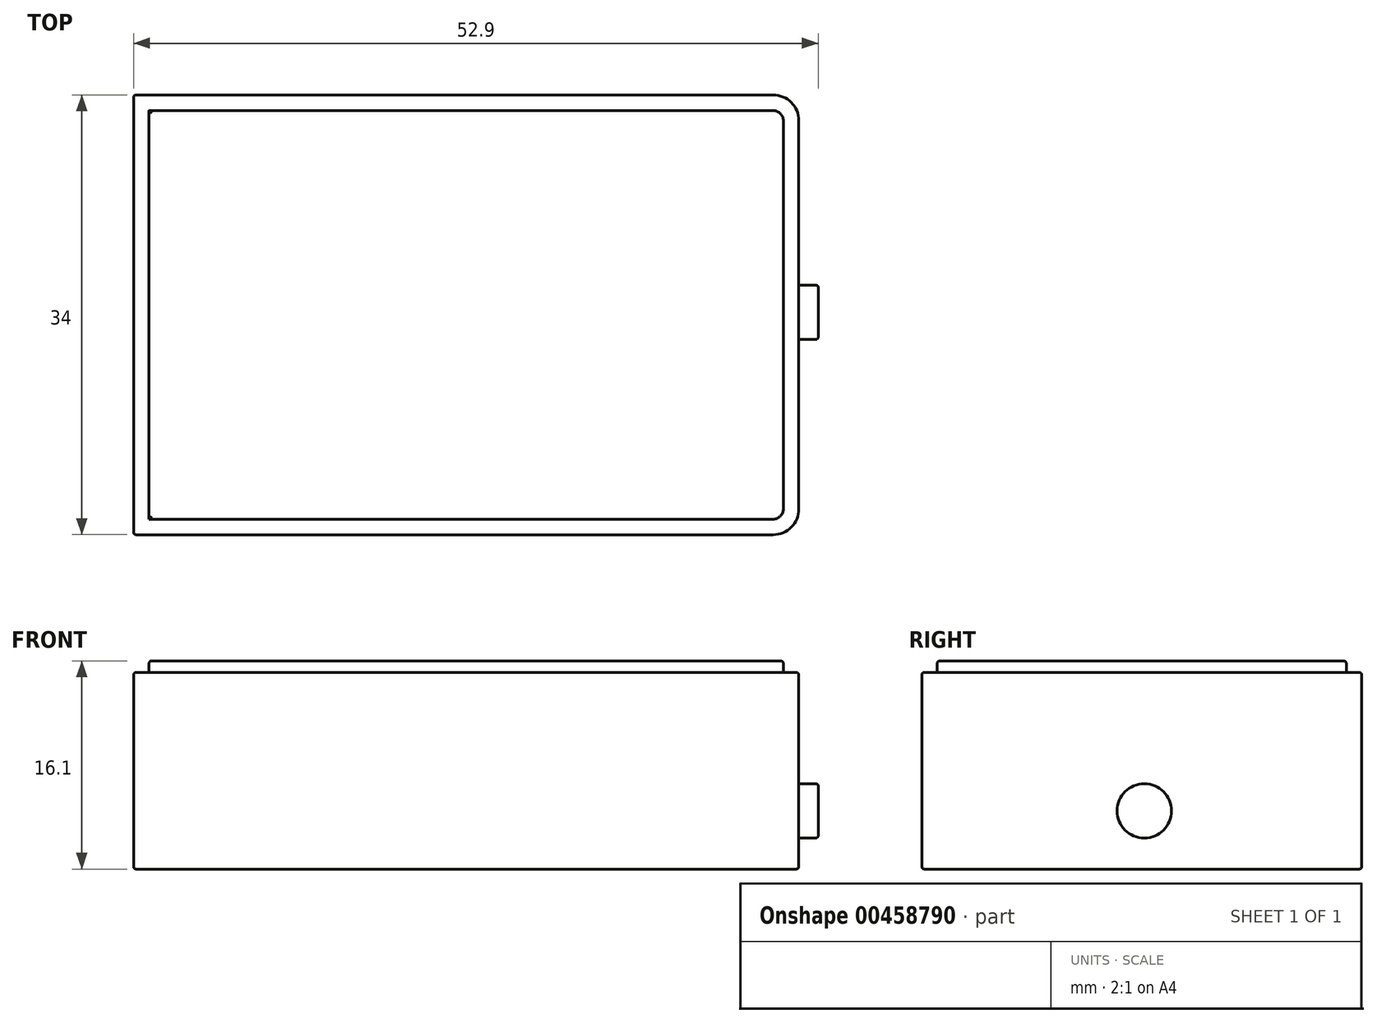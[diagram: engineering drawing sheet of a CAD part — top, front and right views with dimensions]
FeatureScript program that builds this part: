
annotation { "Feature Type Name" : "Feature", "Feature Type Description" : "" }
export const myFeature = defineFeature(function(context is Context, id is Id, definition is map)
    precondition{}
    {
        {
            var Q0;
            Q0=qCreatedBy(makeId("Top.planeOp"),FACE);
            var sketch = newSketch(context, id + "F0", { "sketchPlane" : qUnion([Q0])});
            skLineSegment(sketch, "E0.bottom", {"start": v(-30.33, 20.45) * mm, "end": v(19.07, 20.45) * mm});
            skLineSegment(sketch, "E0.top", {"start": v(-30.33, -13.55) * mm, "end": v(19.07, -13.55) * mm});
            skLineSegment(sketch, "E0.left", {"start": v(-30.33, 20.45) * mm, "end": v(-30.33, -13.55) * mm});
            skLineSegment(sketch, "E0.right", {"start": v(21.07, 18.45) * mm, "end": v(21.07, -11.55) * mm});
            skPoint(sketch, "E1.visualSharp", {"position": v(21.07, 20.45) * mm});
            skArc(sketch, "E1.filletArc", {"start": v(21.07, 18.45) * mm, "mid": v(20.49, 19.86) * mm, "end": v(19.07, 20.45) * mm});
            skPoint(sketch, "E2.visualSharp", {"position": v(21.07, -13.55) * mm});
            skArc(sketch, "E2.filletArc", {"start": v(19.07, -13.55) * mm, "mid": v(20.49, -12.97) * mm, "end": v(21.07, -11.55) * mm});
            skSolve(sketch);
        }
        {
            var Q0;
            Q0=makeQuery(id+"F0.imprint","IMPRINT",FACE,{"disambiguationData":[TD([[makeQuery(id+"F0.imprint","IMPRINT",EDGE,{"derivedFrom":sQuery(id+"F0.wireOp",EDGE,"E0.bottom")}),-1.0]])]});
            extrude(context, id + "F1", {"entities" : qUnion([Q0]), "depth" : 15.2 * mm, "offsetDistance" : 25 * mm});
        }
        {
            var Q0;
            Q0=makeQuery(id+"F1.opExtrude","SWEPT_FACE",FACE,{"disambiguationData":[OSD([sQuery(id+"F0.wireOp",EDGE,"E0.right")])]});
            var sketch = newSketch(context, id + "F2", { "sketchPlane" : qUnion([Q0])});
            skCircle(sketch, "E3", {"center": v(3.65, 4.5) * mm, "radius": 2.1 * mm});
            skSolve(sketch);
        }
        {
            var Q0;
            Q0=makeQuery(id+"F2.imprint","IMPRINT",FACE,{"disambiguationData":[TD([[makeQuery(id+"F2.imprint","IMPRINT",EDGE,{"derivedFrom":sQuery(id+"F2.wireOp",EDGE,"E3")}),1.0]])]});
            extrude(context, id + "F3", {"entities" : qUnion([Q0]), "operationType" : NewBodyOperationType.ADD, "depth" : 1.5 * mm, "offsetDistance" : 25 * mm});
        }
        {
            var Q0;
            Q0=makeQuery(id+"F1.opExtrude","CAP_EDGE",EDGE,{"disambiguationData":[OSD([sQuery(id+"F0.wireOp",EDGE,"E0.right")])],"isStart":false});
            var Q1;
            Q1=makeQuery(id+"F1.opExtrude","CAP_EDGE",EDGE,{"disambiguationData":[OSD([sQuery(id+"F0.wireOp",EDGE,"E0.right")])],"isStart":true});
            var Q2;
            Q2=makeQuery(id+"F3.opExtrude","CAP_EDGE",EDGE,{"disambiguationData":[OSD([sQuery(id+"F2.wireOp",EDGE,"E3")])],"isStart":false});
            var Q3;
            Q3=makeQuery(id+"F3.opExtrude","CAP_EDGE",EDGE,{"disambiguationData":[OSD([sQuery(id+"F2.wireOp",EDGE,"E3")])],"isStart":true});
            var Q4;
            Q4=makeQuery(id+"F1.opExtrude","SWEPT_EDGE",EDGE,{"disambiguationData":[OSD([sQuery(id+"F0.wireOp",EDGE,"E0.bottom"),sQuery(id+"F0.wireOp",EDGE,"E0.left")])]});
            var Q5;
            Q5=makeQuery(id+"F1.opExtrude","SWEPT_EDGE",EDGE,{"disambiguationData":[OSD([sQuery(id+"F0.wireOp",EDGE,"E0.top"),sQuery(id+"F0.wireOp",EDGE,"E0.left")])]});
            var Q6;
            Q6=makeQuery(id+"F1.opExtrude","CAP_EDGE",EDGE,{"disambiguationData":[OSD([sQuery(id+"F0.wireOp",EDGE,"E0.left")])],"isStart":false});
            var Q7;
            Q7=makeQuery(id+"F1.opExtrude","CAP_EDGE",EDGE,{"disambiguationData":[OSD([sQuery(id+"F0.wireOp",EDGE,"E0.left")])],"isStart":true});
            fillet(context, id + "F4", {"entities" : qUnion([Q0, Q1, Q2, Q3, Q4, Q5, Q6, Q7]), "radius" : .2 * mm, "tangentPropagation" : true, "allowEdgeOverflow" : false});
        }
        {
            var Q0;
            Q0=makeQuery(id+"F1.opExtrude","CAP_FACE",FACE,{"disambiguationData":[OSD([sQuery(id+"F0.wireOp",EDGE,"E0.bottom"),sQuery(id+"F0.wireOp",EDGE,"E0.top"),sQuery(id+"F0.wireOp",EDGE,"E0.left"),sQuery(id+"F0.wireOp",EDGE,"E0.right"),sQuery(id+"F0.wireOp",EDGE,"E1.filletArc"),sQuery(id+"F0.wireOp",EDGE,"E2.filletArc")])],"isStart":false});
            var sketch = newSketch(context, id + "F5", { "sketchPlane" : qUnion([Q0])});
            skLineSegment(sketch, "E4.0", {"start": v(-29.13, -12.35) * mm, "end": v(19.07, -12.35) * mm});
            skLineSegment(sketch, "E4.1", {"start": v(19.87, -11.55) * mm, "end": v(19.87, 18.45) * mm});
            skArc(sketch, "E4.2", {"start": v(19.87, 18.45) * mm, "mid": v(19.64, 19.01) * mm, "end": v(19.07, 19.25) * mm});
            skArc(sketch, "E4.3", {"start": v(19.07, -12.35) * mm, "mid": v(19.64, -12.12) * mm, "end": v(19.87, -11.55) * mm});
            skLineSegment(sketch, "E4.4", {"start": v(19.07, 19.25) * mm, "end": v(-29.13, 19.25) * mm});
            skLineSegment(sketch, "E4.5", {"start": v(-29.13, 19.25) * mm, "end": v(-29.13, -12.35) * mm});
            skSolve(sketch);
        }
        {
            var Q0;
            Q0 = qSketchRegion(id + "F5", true);
            extrude(context, id + "F6", {"entities" : qUnion([Q0]), "operationType" : NewBodyOperationType.ADD, "depth" : .9 * mm, "offsetDistance" : 25 * mm});
        }
        {
            var Q0;
            Q0=makeQuery(id+"F6.opExtrude","CAP_EDGE",EDGE,{"disambiguationData":[OSD([sQuery(id+"F5.wireOp",EDGE,"E4.0")])],"isStart":false});
            var Q1;
            Q1=makeQuery(id+"F6.opExtrude","CAP_EDGE",EDGE,{"disambiguationData":[OSD([sQuery(id+"F5.wireOp",EDGE,"E4.3")])],"isStart":false});
            var Q2;
            Q2=makeQuery(id+"F6.opExtrude","CAP_EDGE",EDGE,{"disambiguationData":[OSD([sQuery(id+"F5.wireOp",EDGE,"E4.1")])],"isStart":false});
            var Q3;
            Q3=makeQuery(id+"F6.opExtrude","CAP_EDGE",EDGE,{"disambiguationData":[OSD([sQuery(id+"F5.wireOp",EDGE,"E4.2")])],"isStart":false});
            var Q4;
            Q4=makeQuery(id+"F6.opExtrude","CAP_EDGE",EDGE,{"disambiguationData":[OSD([sQuery(id+"F5.wireOp",EDGE,"E4.4")])],"isStart":false});
            var Q5;
            Q5=makeQuery(id+"F6.opExtrude","CAP_EDGE",EDGE,{"disambiguationData":[OSD([sQuery(id+"F5.wireOp",EDGE,"E4.5")])],"isStart":false});
            fillet(context, id + "F7", {"entities" : qUnion([Q0, Q1, Q2, Q3, Q4, Q5]), "radius" : .2 * mm, "tangentPropagation" : true, "allowEdgeOverflow" : false});
        }
    });
